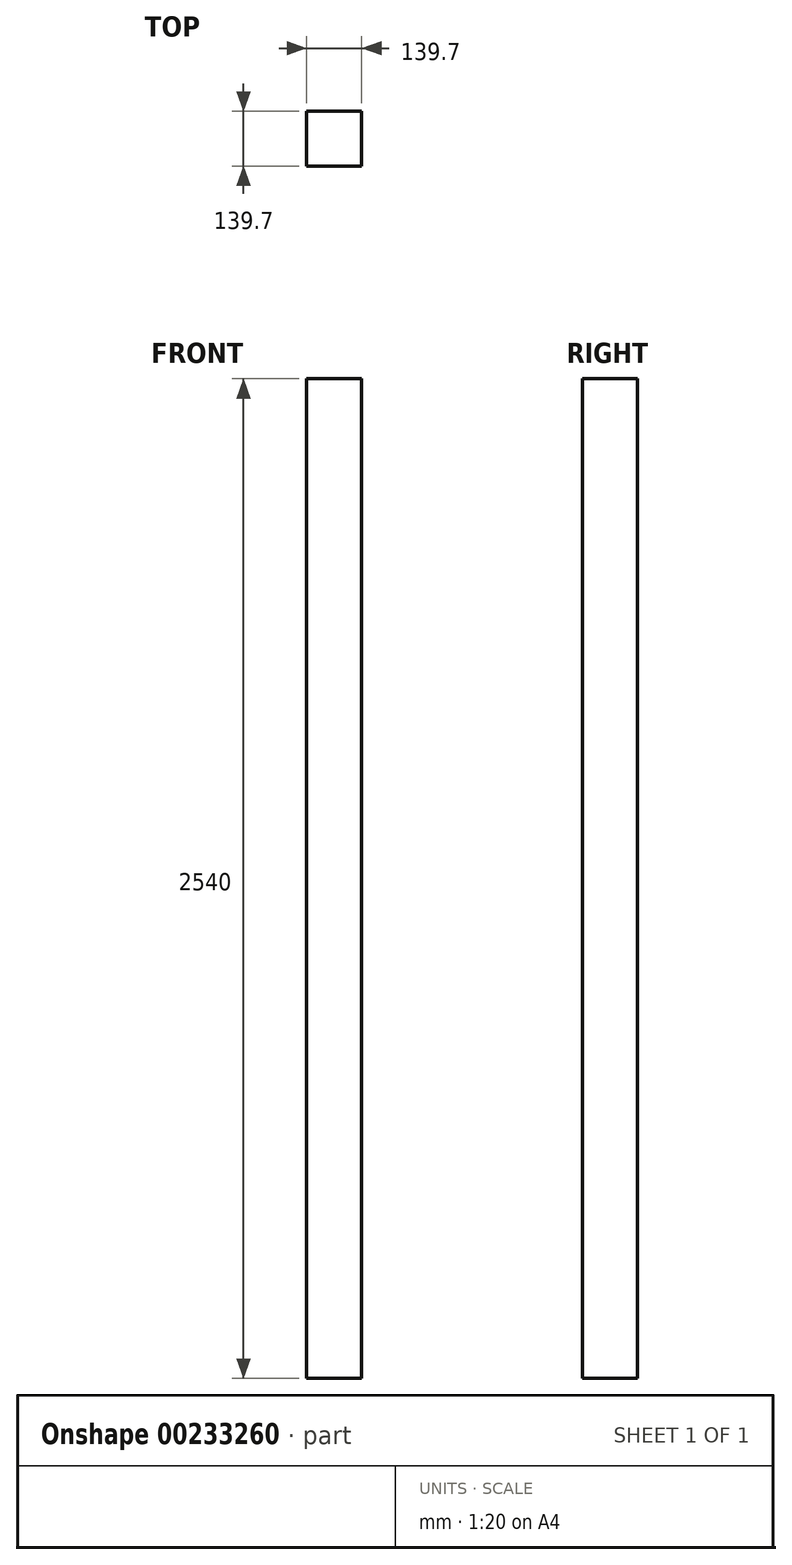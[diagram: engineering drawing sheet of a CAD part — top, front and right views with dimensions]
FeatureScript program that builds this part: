
annotation { "Feature Type Name" : "Feature", "Feature Type Description" : "" }
export const myFeature = defineFeature(function(context is Context, id is Id, definition is map)
    precondition{}
    {
        {
            var Q0;
            Q0=qCreatedBy(makeId("Front.planeOp"),FACE);
            var sketch = newSketch(context, id + "F0", { "sketchPlane" : qUnion([Q0])});
            skLineSegment(sketch, "E0.bottom", {"start": v(-82.53, 2009.08) * mm, "end": v(57.17, 2009.08) * mm});
            skLineSegment(sketch, "E0.top", {"start": v(-82.53, -530.92) * mm, "end": v(57.17, -530.92) * mm});
            skLineSegment(sketch, "E0.left", {"start": v(-82.53, 2009.08) * mm, "end": v(-82.53, -530.92) * mm});
            skLineSegment(sketch, "E0.right", {"start": v(57.17, 2009.08) * mm, "end": v(57.17, -530.92) * mm});
            skSolve(sketch);
        }
        {
            var Q0;
            Q0 = qSketchRegion(id + "F0", true);
            extrude(context, id + "F1", {"entities" : qUnion([Q0]), "depth" : 139.7 * mm});
        }
    });
